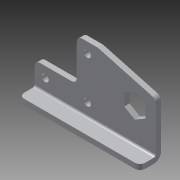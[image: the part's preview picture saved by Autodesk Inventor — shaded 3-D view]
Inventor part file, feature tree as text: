
AUTODESK INVENTOR PART (.ipt)
format: ipt  version: 2014 (Build 180170000, 170)  size: 139,264 bytes
history: native  units: in
note: dims shown in document units (in); Inventor stores cm internally (conversion verified against a paired STEP export)
features: sheet_metal_op x4, sketch x2, other x2, fillet x1
ambient origin geometry x8: Origin, YZ Plane, XZ Plane, XY Plane, X Axis, Y Axis, Z Axis, Center Point
bodies: Solid1 (feature_tree)
feature tree (9):
  sheet_metal_op  "Face1"
  sheet_metal_op  "Flange1"
  fillet  "Fillet2"  Radius=0.5in
  sketch  "Sketch1"  dims[d1=1.0in]
  other  "Plate1"
  sketch  "Sketch2"  dims[d2=1.0in d3=0.5in d4=2.875in d5=0.5in d6=0.75in d7=0.5in d8=90.0deg d9=1.125in d10=0.163in d11=0.25in d12=0.25in d13=0.7874in d15=1.0in d16=0.3937in d18=1.0in d20=0.7874in d22=1.0in d23=0.3937in d25=1.0in d27=0.125in d29=0.125in d30=0.0625in d31=0.25in d32=0.125in d33=0.5in d34=90.0deg d35=0.05in d36=0.5in d37=0.125in d38=0.125in d39=0.125in]
  other  "Plate2"
  sheet_metal_op  "Bend1"
  sheet_metal_op  "Corner1"
